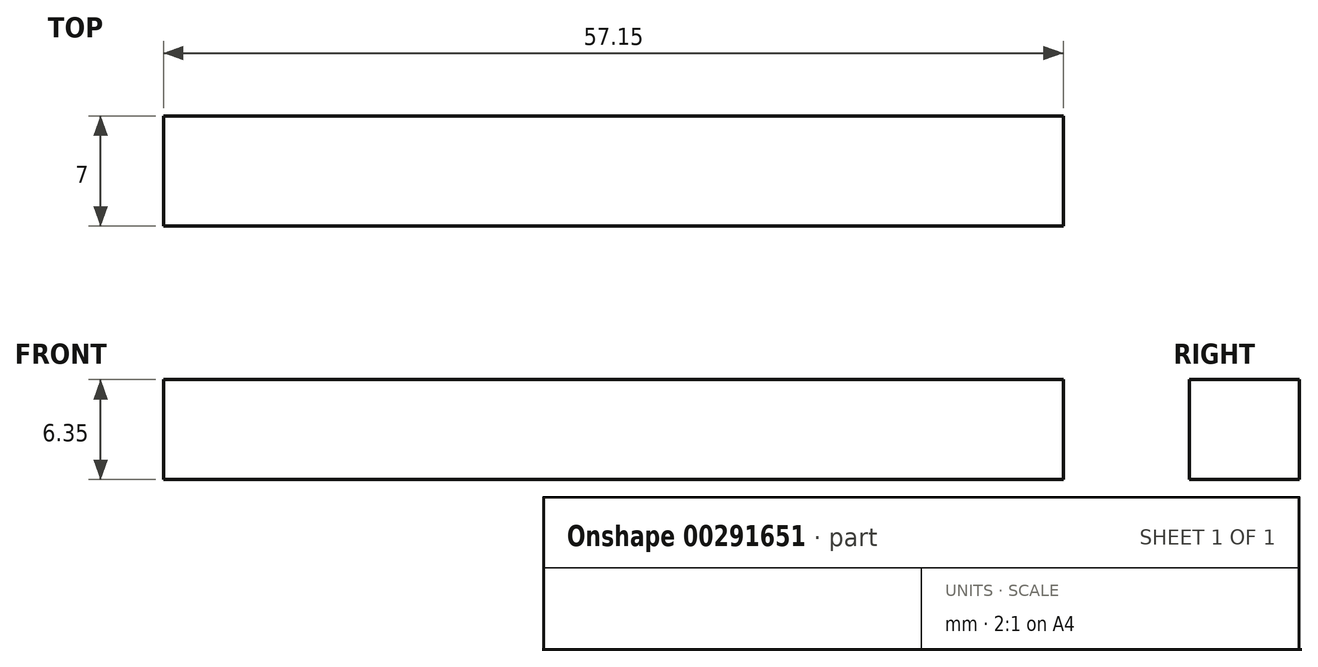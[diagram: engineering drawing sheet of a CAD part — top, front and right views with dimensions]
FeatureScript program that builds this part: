
annotation { "Feature Type Name" : "Feature", "Feature Type Description" : "" }
export const myFeature = defineFeature(function(context is Context, id is Id, definition is map)
    precondition{}
    {
        {
            var Q0;
            Q0=qCreatedBy(makeId("Front.planeOp"),FACE);
            var sketch = newSketch(context, id + "F0", { "sketchPlane" : qUnion([Q0])});
            skLineSegment(sketch, "E0.bottom", {"start": v(-32.33, 6.35) * mm, "end": v(24.82, 6.35) * mm});
            skLineSegment(sketch, "E0.top", {"start": v(-32.33, 0) * mm, "end": v(24.82, 0) * mm});
            skLineSegment(sketch, "E0.left", {"start": v(-32.33, 6.35) * mm, "end": v(-32.33, 0) * mm});
            skLineSegment(sketch, "E0.right", {"start": v(24.82, 6.35) * mm, "end": v(24.82, 0) * mm});
            skSolve(sketch);
        }
        {
            var Q0;
            Q0 = qSketchRegion(id + "F0", true);
            extrude(context, id + "F1", {"entities" : qUnion([Q0]), "endBound" : BoundingType.SYMMETRIC, "depth" : 7 * mm});
        }
    });
